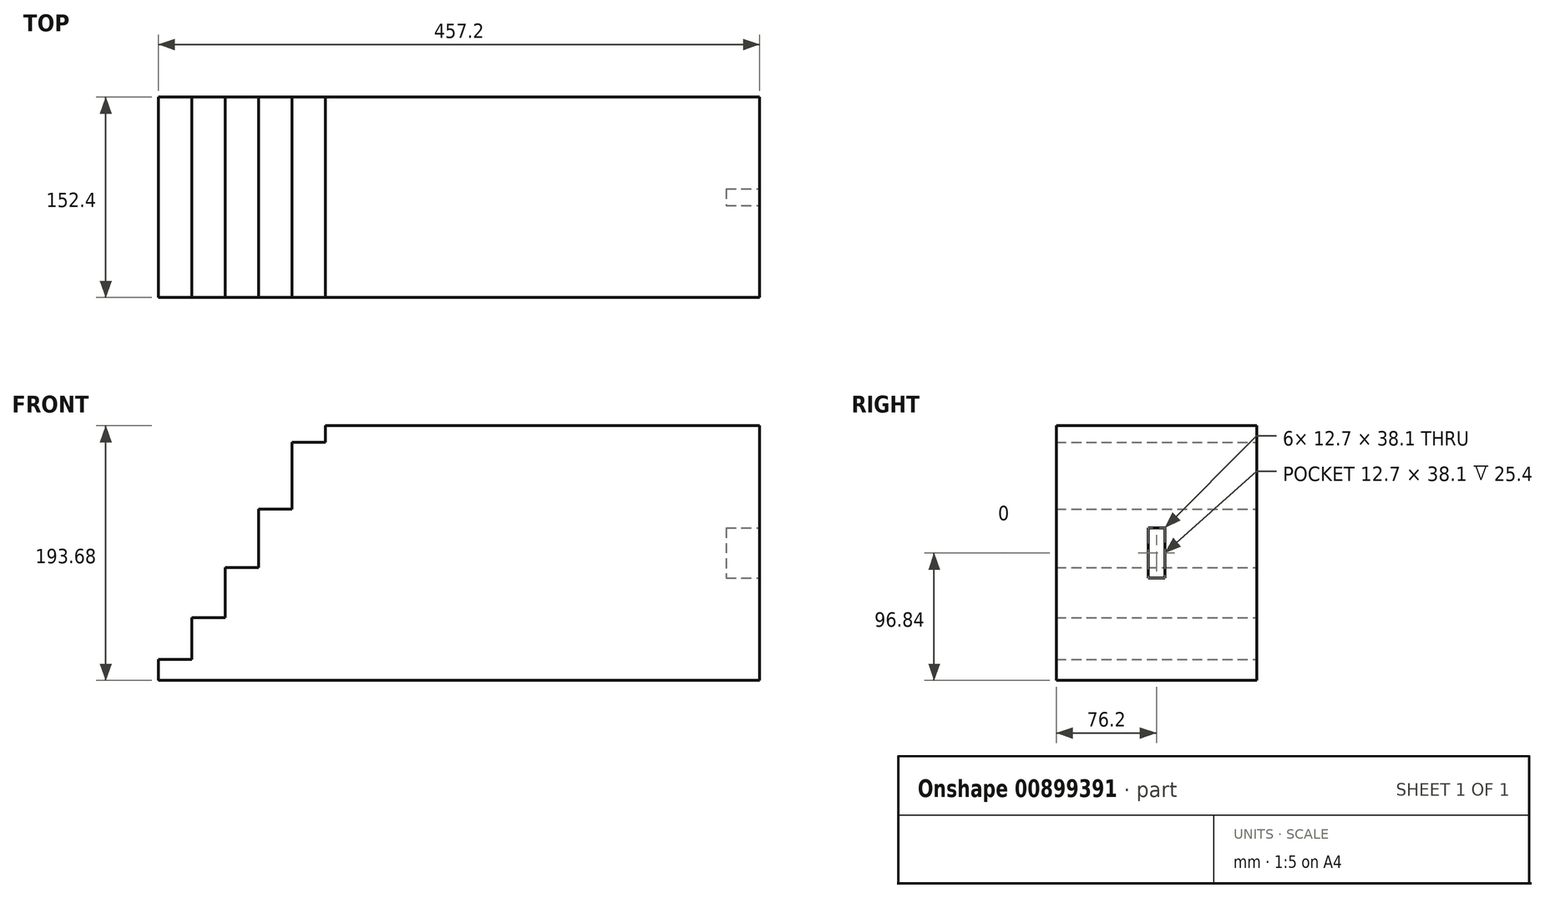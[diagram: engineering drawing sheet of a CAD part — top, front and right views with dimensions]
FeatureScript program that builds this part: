
annotation { "Feature Type Name" : "Feature", "Feature Type Description" : "" }
export const myFeature = defineFeature(function(context is Context, id is Id, definition is map)
    precondition{}
    {
        {
            var Q0;
            Q0=qCreatedBy(makeId("Front.planeOp"),FACE);
            var sketch = newSketch(context, id + "F0", { "sketchPlane" : qUnion([Q0])});
            skLineSegment(sketch, "E0.bottom", {"start": v(228.6, 96.84) * mm, "end": v(-228.6, 96.84) * mm});
            skLineSegment(sketch, "E0.top", {"start": v(228.6, -96.84) * mm, "end": v(-228.6, -96.84) * mm});
            skLineSegment(sketch, "E0.left", {"start": v(228.6, 96.84) * mm, "end": v(228.6, -96.84) * mm});
            skLineSegment(sketch, "E0.right", {"start": v(-228.6, 96.84) * mm, "end": v(-228.6, -96.84) * mm});
            skPoint(sketch, "E0.middle", {"position": v(0, 0) * mm});
            skLineSegment(sketch, "E1", {"start": v(-228.6, -80.96) * mm, "end": v(-203.2, -80.96) * mm});
            skLineSegment(sketch, "E2", {"start": v(-203.2, -80.96) * mm, "end": v(-203.2, -49.21) * mm});
            skLineSegment(sketch, "E3", {"start": v(-203.2, -49.21) * mm, "end": v(-177.8, -49.21) * mm});
            skLineSegment(sketch, "E4", {"start": v(-177.8, -49.21) * mm, "end": v(-177.8, -11.11) * mm});
            skLineSegment(sketch, "E5", {"start": v(-177.8, -11.11) * mm, "end": v(-152.4, -11.11) * mm});
            skLineSegment(sketch, "E6", {"start": v(-152.4, -11.11) * mm, "end": v(-152.4, 33.34) * mm});
            skLineSegment(sketch, "E7", {"start": v(-152.4, 33.34) * mm, "end": v(-127, 33.34) * mm});
            skLineSegment(sketch, "E8", {"start": v(-127, 84.14) * mm, "end": v(-101.6, 84.14) * mm});
            skLineSegment(sketch, "E9", {"start": v(-101.6, 84.14) * mm, "end": v(-101.6, 96.84) * mm});
            skLineSegment(sketch, "E10", {"start": v(-127, 84.14) * mm, "end": v(-127, 33.34) * mm});
            skSolve(sketch);
        }
        {
            var Q0;
            {var subQ5=sQuery(id+"F0.wireOp",EDGE,"E0.top");Q0=makeQuery(id+"F0.imprint","IMPRINT",FACE,{"disambiguationData":[TD([[makeQuery(id+"F0.imprint","IMPRINT",EDGE,{"derivedFrom":subQ5}),-1.0]])]});}
            extrude(context, id + "F1", {"entities" : qUnion([Q0]), "depth" : 152.4 * mm, "offsetDistance" : 25.4 * mm});
        }
        {
            var Q0;
            Q0=makeQuery(id+"F1.opExtrude","SWEPT_FACE",FACE,{"disambiguationData":[OSD([sQuery(id+"F0.wireOp",EDGE,"E0.left")])]});
            var sketch = newSketch(context, id + "F2", { "sketchPlane" : qUnion([Q0])});
            skLineSegment(sketch, "E11", {"start": v(-152.4, 96.84) * mm, "end": v(0, -96.84) * mm});
            skLineSegment(sketch, "E12", {"start": v(0, 96.84) * mm, "end": v(-152.4, -96.84) * mm});
            skLineSegment(sketch, "E13.bottom", {"start": v(-69.85, 19.05) * mm, "end": v(-82.55, 19.05) * mm});
            skLineSegment(sketch, "E13.top", {"start": v(-69.85, -19.05) * mm, "end": v(-82.55, -19.05) * mm});
            skLineSegment(sketch, "E13.left", {"start": v(-69.85, 19.05) * mm, "end": v(-69.85, -19.05) * mm});
            skLineSegment(sketch, "E13.right", {"start": v(-82.55, 19.05) * mm, "end": v(-82.55, -19.05) * mm});
            skPoint(sketch, "E13.middle", {"position": v(-76.2, 0) * mm});
            skSolve(sketch);
        }
        {
            var Q0;
            Q0 = qSketchRegion(id + "F2", true);
            extrude(context, id + "F3", {"entities" : qUnion([Q0]), "operationType" : NewBodyOperationType.REMOVE, "oppositeDirection" : true, "depth" : 25.4 * mm, "offsetDistance" : 25.4 * mm});
        }
    });
